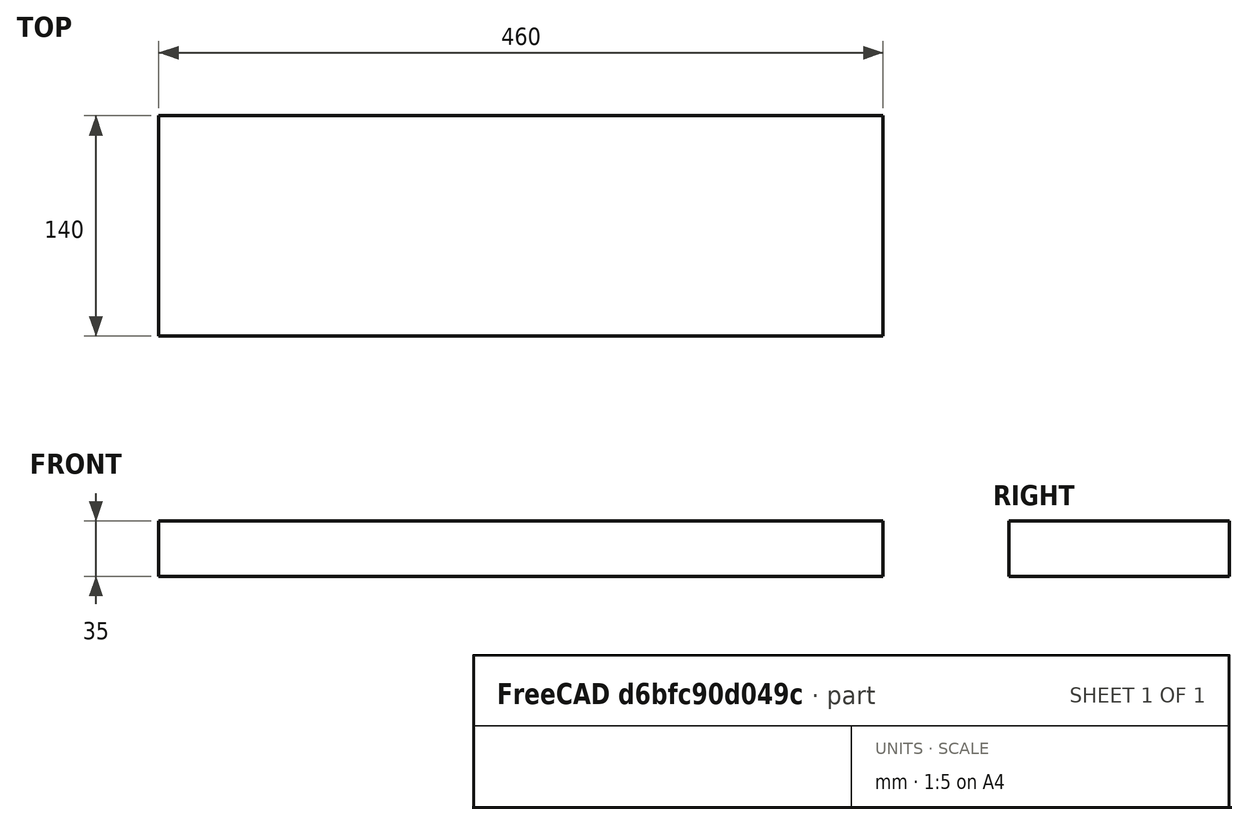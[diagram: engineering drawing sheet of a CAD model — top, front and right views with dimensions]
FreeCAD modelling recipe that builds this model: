
FCSTD DOCUMENT  (FreeCAD 0.18R4 (GitTag))
Label: top_stretcher
License: All rights reserved
LicenseURL: http://en.wikipedia.org/wiki/All_rights_reserved
objects: Sketcher::SketchObject×1, PartDesign::Pad×1, PartDesign::Body×1
note: 4 computed .brp shape members not serialized (recipe doc carries the construction recipe); baked Part::Feature solids carry a one-line shape summary decoded from their .brp

FEATURE [Sketcher::SketchObject] Sketch
  MapMode = 5
  Placement = pos=(0,0,0) rot=(0.57735,0.57735,0.57735;2.0944rad)
  Support = -> [YZ_Plane]
  sketch-geometry (4):
    g0: LineSegment StartX=0 StartY=0 StartZ=0 EndX=-140 EndY=0 EndZ=0
    g1: LineSegment StartX=-140 StartY=0 StartZ=0 EndX=-140 EndY=35 EndZ=0
    g2: LineSegment StartX=-140 StartY=35 StartZ=0 EndX=0 EndY=35 EndZ=0
    g3: LineSegment StartX=0 StartY=35 StartZ=0 EndX=0 EndY=0 EndZ=0
  constraints (11):
    c: Coincident(g0,g1)
    c: Coincident(g1,g2)
    c: Coincident(g2,g3)
    c: Coincident(g3,g0)
    c: Horizontal(g0)
    c: Horizontal(g2)
    c: Vertical(g1)
    c: Vertical(g3)
    c: Coincident(g0,g-1)
    c: DistanceY(g3,g3) = 35
    c: DistanceX(g0,g0) = 140
FEATURE [PartDesign::Pad] Pad
  Length = 460
  Length2 = 100
  Placement = pos=(0,0,0) rot=(0.57735,0.57735,0.57735;2.0944rad)
  Profile = -> Sketch
  Type = 0
FEATURE [PartDesign::Body] Body
  Group = -> [Sketch,Pad]
  Origin = -> Origin
  Tip = -> Pad
